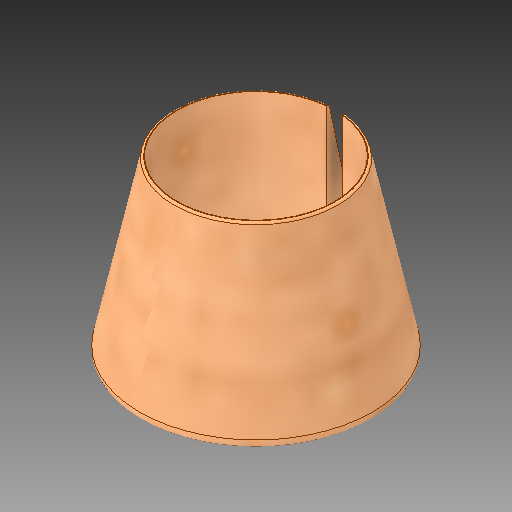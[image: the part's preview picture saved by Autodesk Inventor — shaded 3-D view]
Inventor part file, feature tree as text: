
AUTODESK INVENTOR PART (.ipt)
format: ipt  version: 2018 (Build 220112000, 112)  size: 223,232 bytes
history: native  units: mm
features: sketch x2, revolve x1, extrude x1
ambient origin geometry x8: Origin, YZ Plane, XZ Plane, XY Plane, X Axis, Y Axis, Z Axis, Center Point
bodies: Solid1 (feature_tree)
feature tree (4):
  revolve  "Revolution1"  [1 undecoded]
  extrude  "Extrusion1"  Depth=1.0mm
  sketch  "Sketch1"  dims[d0=11.0mm d1=2.094395mm]
  sketch  "Sketch2"  dims[d2=5.16mm d3=5.0mm d4=1.5mm d6=45.0deg d7=7.498122mm d8=0.5mm d9=0.15mm d10=90.0deg d11=1.0mm d12=6.39mm d13=10.0mm d14=0.0mm]
note: 1 required parameter value undecoded (feature->parameter linkage not recoverable at this tier; creation-order binding heuristic only, values carry confidence <= 0.55)
